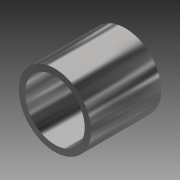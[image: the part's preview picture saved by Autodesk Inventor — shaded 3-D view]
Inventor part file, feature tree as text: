
AUTODESK INVENTOR PART (.ipt)
format: ipt  version: 2013 (Build 170138000, 138)  size: 89,600 bytes
history: native  units: in
note: dims shown in document units (in); Inventor stores cm internally (conversion verified against a paired STEP export)
features: extrude x1, sketch x1
ambient origin geometry x8: Origin, YZ Plane, XZ Plane, XY Plane, X Axis, Y Axis, Z Axis, Center Point
bodies: Solid1 (feature_tree)
feature tree (2):
  extrude  "Extrusion1"  Depth=1.94in
  sketch  "Sketch1"  dims[d0=2.35in d2=1.94in d3=2.285in d4=0.0in]
